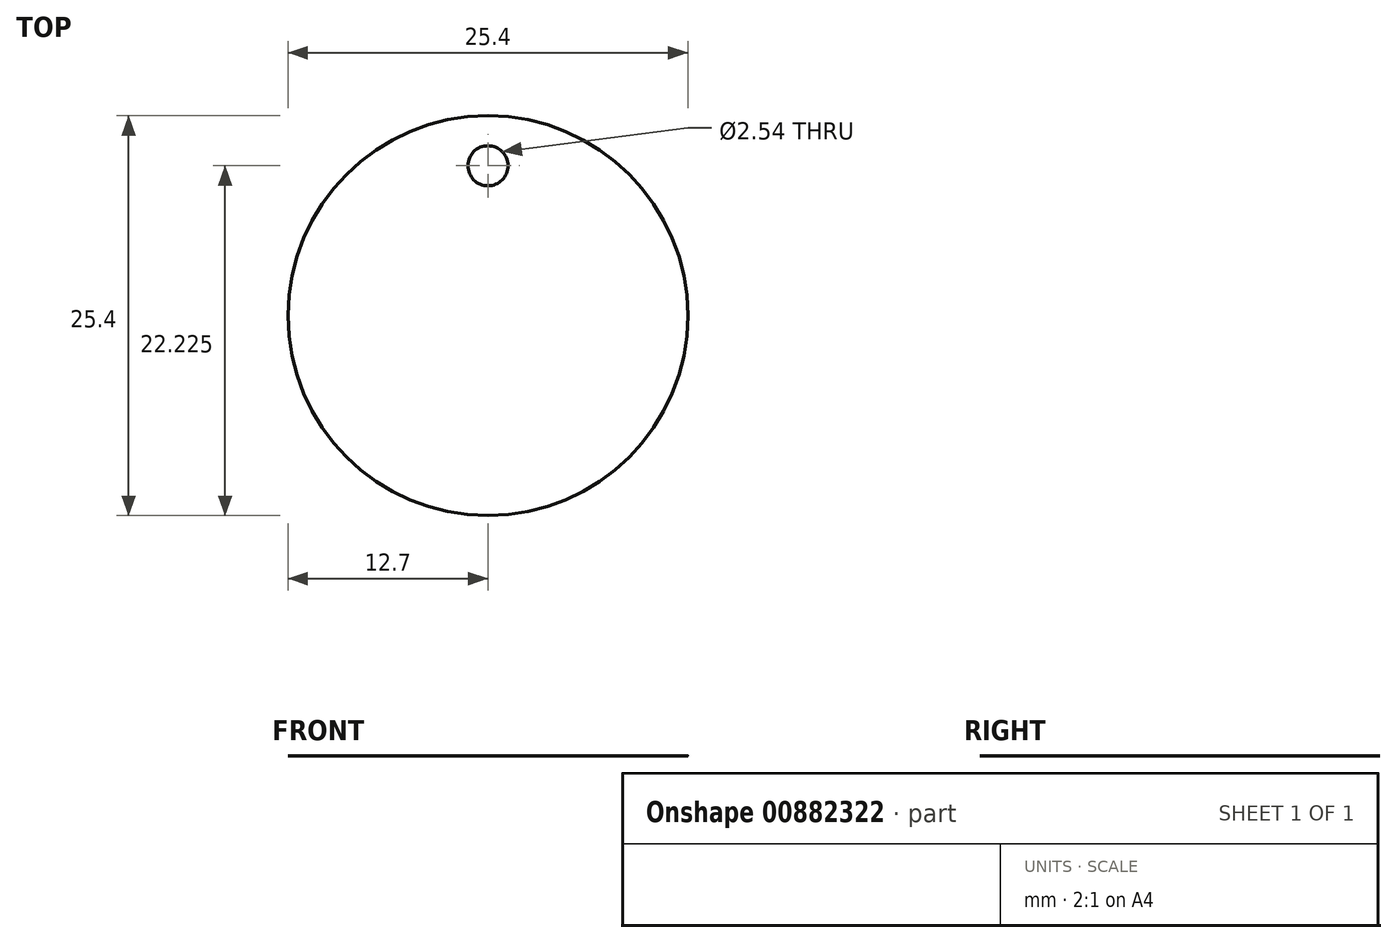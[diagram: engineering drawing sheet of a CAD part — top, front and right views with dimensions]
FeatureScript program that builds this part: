
annotation { "Feature Type Name" : "Feature", "Feature Type Description" : "" }
export const myFeature = defineFeature(function(context is Context, id is Id, definition is map)
    precondition{}
    {
        {
            var Q0;
            Q0=qCreatedBy(makeId("Top.planeOp"),FACE);
            var sketch = newSketch(context, id + "F0", { "sketchPlane" : qUnion([Q0])});
            skCircle(sketch, "E0", {"center": v(0, 0) * mm, "radius": 12.7 * mm});
            skSolve(sketch);
        }
        {
            var Q0;
            Q0 = qSketchRegion(id + "F0", true);
            extrude(context, id + "F1", {"entities" : qUnion([Q0]), "depth" : 1 / 203.2 * mm, "offsetDistance" : 25.4 * mm});
        }
        {
            var Q0;
            Q0=makeQuery(id+"F1.opExtrude","CAP_FACE",FACE,{"disambiguationData":[OSD([sQuery(id+"F0.wireOp",EDGE,"E0")])],"isStart":false});
            var sketch = newSketch(context, id + "F2", { "sketchPlane" : qUnion([Q0])});
            skPoint(sketch, "E1", {"position": v(0, 12.7) * mm});
            skPoint(sketch, "E2", {"position": v(0, 6.35) * mm});
            skCircle(sketch, "E3", {"center": v(0, 9.53) * mm, "radius": 1.27 * mm});
            skSolve(sketch);
        }
        {
            var Q0;
            Q0 = qSketchRegion(id + "F2", true);
            extrude(context, id + "F3", {"entities" : qUnion([Q0]), "operationType" : NewBodyOperationType.REMOVE, "oppositeDirection" : true, "depth" : 25.4 * mm, "offsetDistance" : 25.4 * mm});
        }
    });
